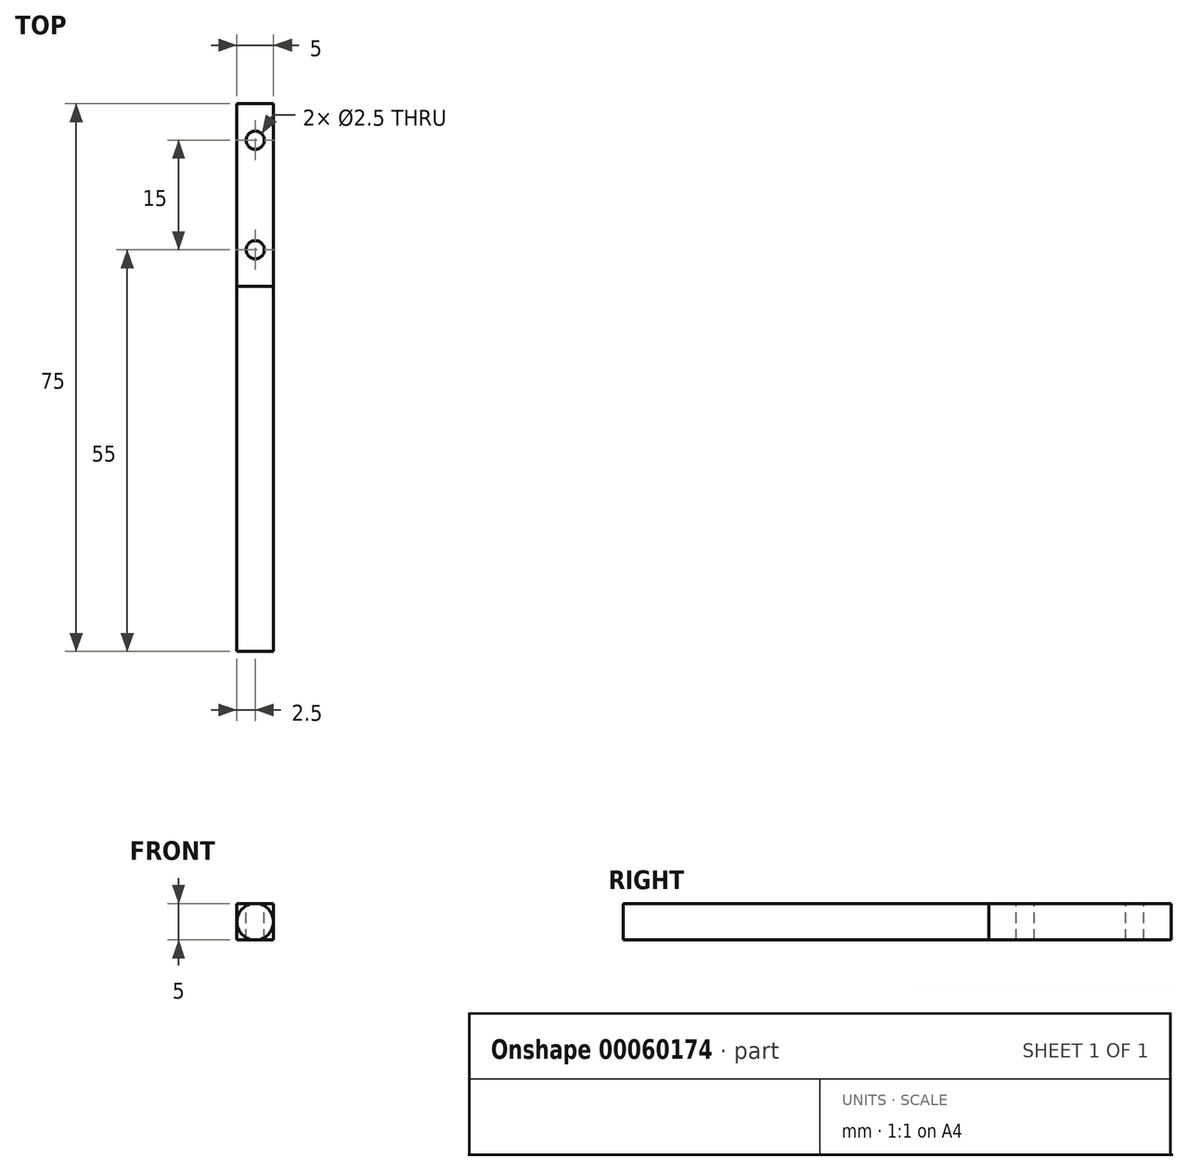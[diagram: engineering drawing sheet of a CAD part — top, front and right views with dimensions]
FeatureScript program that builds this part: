
annotation { "Feature Type Name" : "Feature", "Feature Type Description" : "" }
export const myFeature = defineFeature(function(context is Context, id is Id, definition is map)
    precondition{}
    {
        {
            var Q0;
            Q0=qCreatedBy(makeId("Front.planeOp"),FACE);
            var sketch = newSketch(context, id + "F0", { "sketchPlane" : qUnion([Q0])});
            skLineSegment(sketch, "E0.bottom", {"start": v(-2.5, 2.5) * mm, "end": v(2.5, 2.5) * mm});
            skLineSegment(sketch, "E0.top", {"start": v(-2.5, -2.5) * mm, "end": v(2.5, -2.5) * mm});
            skLineSegment(sketch, "E0.left", {"start": v(-2.5, 2.5) * mm, "end": v(-2.5, -2.5) * mm});
            skLineSegment(sketch, "E0.right", {"start": v(2.5, 2.5) * mm, "end": v(2.5, -2.5) * mm});
            skSolve(sketch);
        }
        {
            var Q0;
            Q0=qSketchRegion(id+"F0",true);
            extrude(context, id + "F1", {"entities" : qUnion([Q0]), "depth" : 25 * mm});
        }
        {
            var Q0;
            Q0=makeQuery(id+"F1.opExtrude","CAP_FACE",FACE,{"disambiguationData":[OSD([sQuery(id+"F0.wireOp",EDGE,"E0.bottom"),sQuery(id+"F0.wireOp",EDGE,"E0.top"),sQuery(id+"F0.wireOp",EDGE,"E0.left"),sQuery(id+"F0.wireOp",EDGE,"E0.right")])],"isStart":false});
            var sketch = newSketch(context, id + "F2", { "sketchPlane" : qUnion([Q0])});
            skCircle(sketch, "E1", {"center": v(0, 0) * mm, "radius": 2.5 * mm});
            skSolve(sketch);
        }
        {
            var Q0;
            Q0=qSketchRegion(id+"F2",true);
            extrude(context, id + "F3", {"entities" : qUnion([Q0]), "operationType" : NewBodyOperationType.ADD, "depth" : 50 * mm});
        }
        {
            var Q0;
            Q0=makeQuery(id+"F1.opExtrude","SWEPT_FACE",FACE,{"disambiguationData":[OSD([sQuery(id+"F0.wireOp",EDGE,"E0.bottom")])]});
            var sketch = newSketch(context, id + "F4", { "sketchPlane" : qUnion([Q0])});
            skCircle(sketch, "E2", {"center": v(0, -5) * mm, "radius": 1.25 * mm});
            skCircle(sketch, "E3", {"center": v(0, -20) * mm, "radius": 1.25 * mm});
            skSolve(sketch);
        }
        {
            var Q0;
            Q0=qSketchRegion(id+"F4",true);
            extrude(context, id + "F5", {"entities" : qUnion([Q0]), "operationType" : NewBodyOperationType.REMOVE, "oppositeDirection" : true, "depth" : 25 * mm});
        }
    });
